# Revit family: BC_Hitachi_Samurai-M-304050-F_LOD400_
name_source: partatom
category: Mechanical Equipment
revit_build: Autodesk Revit 2018 (Build: 20170223_1515(x64)
units: mm (PartAtom-declared; Revit-internal decimal feet)

## family parameters
Always vertical = Yes
Classification = None
Cut with Voids When Loaded = No
Part Type = Normal
Room Calculation Point = No
Round Connector Dimension = Use Diameter
Shared = No
Work Plane-Based = No

## types (3) — shared parameters
BC_OBJECT_ID = 205378
BC_OBJECT_VERSION = #31
Description = Samurai M - Heat Pump Inverter Scroll. RHMA 18AN-F - RHMA 50AN-F
Frequency = 50 Hz
Inlet Water Diameter = 64 mm
Manufacturer = Hitachi Air Conditioning Europe SAS
MasterFormat = Central HVAC Equipment
Masterformat Code = 23 70 00
Model = Samurai M - Heat Pump Inverter Scroll (Inc. F/S Pump)
Name BIM&CO = Outdoor Unit
Nominal Voltage = 400 V
Number of Poles = 3
OmniClass code = 23-33 21 13
OmniClass description = Chillers
Operating mode = Heating+Cooling
Overall height = 2440 mm
Overall length = 2240 mm
Overall width = 1200 mm
Refrigerant Type = R410A
Uniformat = Cooling Generating Systems
Uniformat code = D3030
Water Outlet Diameter = 64 mm

## per-type parameters (varying)
| type | Airflow (High) | BC_VARIANT_ID | Coefficient of Performance (COP) | Cooling Capacity | Cooling Input Rated | Energy efficiency SCOP | Energy efficiency ratio (EER) | Heating Capacity | Heating Input Rated | Load of Refrigerant Fluid | Packing Weight | Rated Cooling Current | SEER energy efficiency | Sound Power (Cooling) | Sound Power (Heating) | Sound Pressure at 10m (Cooling) | Sound Pressure at 1m (Cooling) | Starting current | Weight in operation |
| RHMA 30AN-F | 9018.3 L/s | 494328 | 3.09 | 78200 W | 24800 W | 3.4 | 3.15 | 86800 W | 28100 W | 17.60 kg | 1131.00 kg | 48 A | 4.43 | 81 | 84 | 52 | 66 | 163 A | 1105.00 kg |
| RHMA 40AN-F | 10082.2 L/s | 494329 | 3.01 | 99100 W | 32600 W | 3.41 | 3.04 | 98700 W | 32800 W | 20.50 kg | 1156.00 kg | 61 A | 4.24 | 83 | 85 | 54 | 68 | 199 A | 1132.00 kg |
| RHMA 50AN-F | 11707.8 L/s | 494330 | 2.78 | 122800 W | 40800 W | 3.54 | 3.01 | 131500 W | 47300 W | 22.80 kg | 1235.00 kg | 79 A | 4.42 | 84 | 89 | 55 | 69 | 212 A | 1211.00 kg |

note: column(s) folded — value = type name in every type: Product Code, Reference

## geometry (parser evidence)
native form markers: Blend x2
no freeform markers — native parametric forms only
